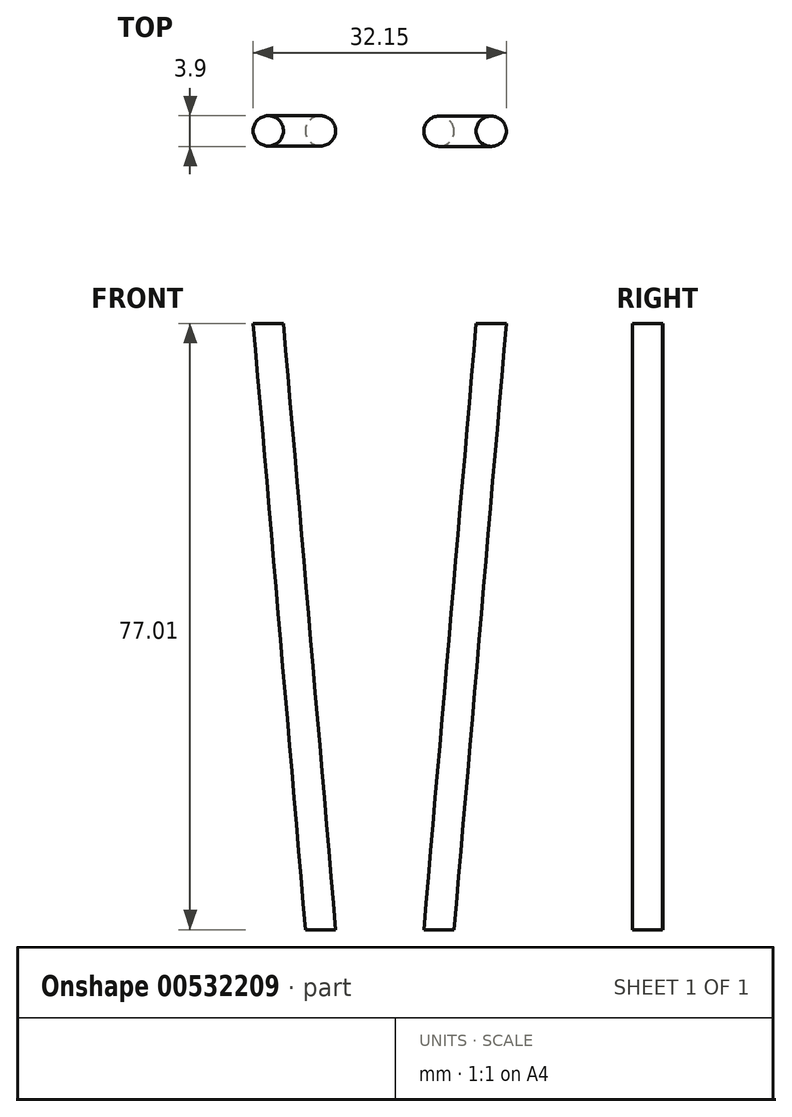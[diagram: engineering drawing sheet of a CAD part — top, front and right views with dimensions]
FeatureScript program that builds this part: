
annotation { "Feature Type Name" : "Feature", "Feature Type Description" : "" }
export const myFeature = defineFeature(function(context is Context, id is Id, definition is map)
    precondition{}
    {
        {
            var Q0;
            Q0=qCreatedBy(makeId("Front.planeOp"),FACE);
            var sketch = newSketch(context, id + "F0", { "sketchPlane" : qUnion([Q0])});
            skArc(sketch, "E0", {"start": v(-7.5, 0) * mm, "mid": v(0, -28) * mm, "end": v(7.5, 0) * mm});
            skLineSegment(sketch, "E1", {"start": v(-7.5, 0) * mm, "end": v(-14.14, 77) * mm});
            skLineSegment(sketch, "E2", {"start": v(0, -13) * mm, "end": v(0, 71.91) * mm, "construction": true});
            skLineSegment(sketch, "E3.MirrorCS", {"start": v(7.5, 0) * mm, "end": v(14.14, 77) * mm});
            skLineSegment(sketch, "E4", {"start": v(-15, 87) * mm, "end": v(15, 87) * mm, "construction": true});
            skLineSegment(sketch, "E5", {"start": v(-14.14, 77) * mm, "end": v(14.14, 77) * mm, "construction": true});
            skSolve(sketch);
        }
        {
            var Q0;
            Q0=sQuery(id+"F0.wireOp",EDGE,"E1");
            var Q1;
            Q1=sQuery(id+"F0.wireOp",EDGE,"E0");
            var Q2;
            Q2=sQuery(id+"F0.wireOp",EDGE,"E3.MirrorCS");
            var Q3;
            Q3=sQuery(id+"F0.wireOp",EDGE,"E4");
            revolve(context, id + "F1", {"bodyType" : ToolBodyType.SURFACE, "surfaceEntities" : qUnion([Q0, Q1, Q2]), "axis" : qUnion([Q3]), "revolveType" : RevolveType.ONE_DIRECTION, "angle" : 15 * degree});
        }
        {
            var Q0;
            Q0=qCreatedBy(makeId("Top.planeOp"),FACE);
            var sketch = newSketch(context, id + "F2", { "sketchPlane" : qUnion([Q0])});
            skCircle(sketch, "E6", {"center": v(-7.52, 1.92) * mm, "radius": 1.92 * mm});
            skCircle(sketch, "E7", {"center": v(7.53, 1.87) * mm, "radius": 1.92 * mm});
            skSolve(sketch);
        }
        {
            var Q0;
            Q0=makeQuery(id+"F2.imprint","IMPRINT",FACE,{"disambiguationData":[TD([[makeQuery(id+"F2.imprint","IMPRINT",EDGE,{"derivedFrom":sQuery(id+"F2.wireOp",EDGE,"E6")}),1.0]])]});
            var Q1;
            Q1=makeQuery(id+"F1.opRevolve","CAP_EDGE",EDGE,{"disambiguationData":[OSD([sQuery(id+"F0.wireOp",EDGE,"E1")])],"isStart":true});
            sweep(context, id + "F3", {"profiles" : qUnion([Q0]), "path" : qUnion([Q1])});
        }
        {
            var Q0;
            Q0=makeQuery(id+"F2.imprint","IMPRINT",FACE,{"disambiguationData":[TD([[makeQuery(id+"F2.imprint","IMPRINT",EDGE,{"derivedFrom":sQuery(id+"F2.wireOp",EDGE,"E7")}),1.0]])]});
            var Q1;
            Q1=makeQuery(id+"F1.opRevolve","CAP_EDGE",EDGE,{"disambiguationData":[OSD([sQuery(id+"F0.wireOp",EDGE,"E3.MirrorCS")])],"isStart":true});
            sweep(context, id + "F4", {"profiles" : qUnion([Q0]), "path" : qUnion([Q1])});
        }
    });
